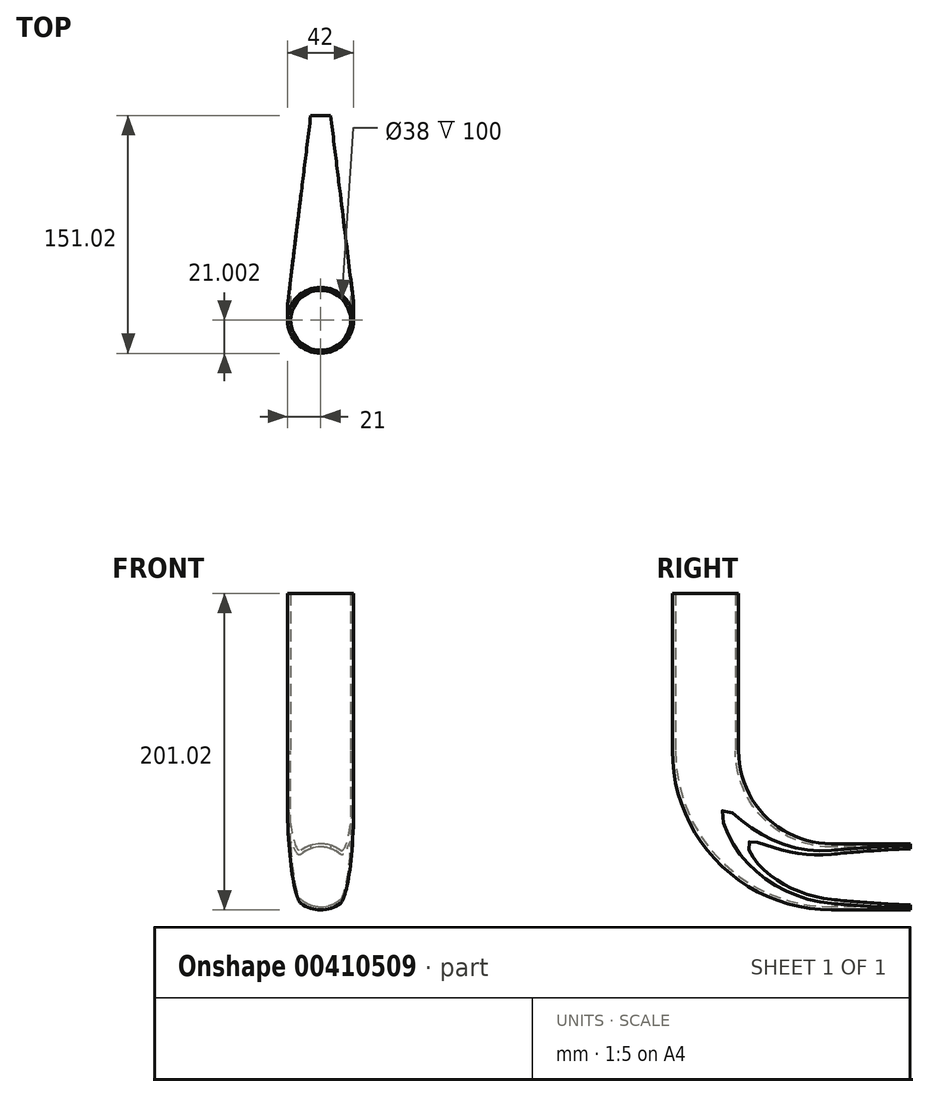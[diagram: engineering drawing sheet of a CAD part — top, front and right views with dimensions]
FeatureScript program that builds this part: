
annotation { "Feature Type Name" : "Feature", "Feature Type Description" : "" }
export const myFeature = defineFeature(function(context is Context, id is Id, definition is map)
    precondition{}
    {
        {
            var Q0;
            Q0=qCreatedBy(makeId("Right.planeOp"),FACE);
            var sketch = newSketch(context, id + "F0", { "sketchPlane" : qUnion([Q0])});
            skArc(sketch, "E0", {"start": v(0, -80) * mm, "mid": v(-56.57, -56.57) * mm, "end": v(-80, 0) * mm});
            skSolve(sketch);
        }
        {
            var Q0;
            Q0=qCreatedBy(makeId("Top.planeOp"),FACE);
            var sketch = newSketch(context, id + "F1", { "sketchPlane" : qUnion([Q0])});
            skCircle(sketch, "E1", {"center": v(0, -80.02) * mm, "radius": 21 * mm});
            skCircle(sketch, "E2", {"center": v(0, -80.02) * mm, "radius": 19 * mm});
            skSolve(sketch);
        }
        {
            var Q0;
            Q0=makeQuery(id+"F1.imprint","IMPRINT",FACE,{"disambiguationData":[TD([[makeQuery(id+"F1.imprint","IMPRINT",EDGE,{"derivedFrom":sQuery(id+"F1.wireOp",EDGE,"E1")}),1.0]])]});
            var Q1;
            Q1=sQuery(id+"F0.wireOp",EDGE,"E0");
            sweep(context, id + "F2", {"profiles" : qUnion([Q0]), "path" : qUnion([Q1])});
        }
        {
            var Q0;
            Q0=makeQuery(id+"F2.opSweep","CAP_FACE",FACE,{"disambiguationData":[OSD([sQuery(id+"F0.wireOp",VERTEX,"E0.end"),sQuery(id+"F1.wireOp",EDGE,"E1"),sQuery(id+"F1.wireOp",EDGE,"E2")])],"isStart":true});
            extrude(context, id + "F3", {"entities" : qUnion([Q0]), "operationType" : NewBodyOperationType.ADD, "depth" : 100 * mm});
        }
        {
            var Q0;
            Q0=makeQuery(id+"F2.opSweep","CAP_FACE",FACE,{"disambiguationData":[OSD([sQuery(id+"F0.wireOp",VERTEX,"E0.start"),sQuery(id+"F1.wireOp",EDGE,"E1"),sQuery(id+"F1.wireOp",EDGE,"E2")])],"isStart":false});
            extrude(context, id + "F4", {"entities" : qUnion([Q0]), "operationType" : NewBodyOperationType.ADD, "depth" : 50 * mm});
        }
        {
            var Q0;
            Q0=makeQuery(id+"F4.opExtrude","SWEPT_FACE",FACE,{"disambiguationData":[OSD([sQuery(id+"F0.wireOp",VERTEX,"E0.start"),sQuery(id+"F1.wireOp",EDGE,"E2")])]});
            cPlane(context, id + "F5", {"entities" : qUnion([Q0]), "cplaneType" : CPlaneType.LINE_ANGLE, "offset" : 25 * mm, "angle" : 0 * degree, "width" : 150 * mm, "height" : 150 * mm});
        }
        {
            var Q0;
            Q0=qCreatedBy(id+"F5.planeOp",FACE);
            var sketch = newSketch(context, id + "F6", { "sketchPlane" : qUnion([Q0])});
            skLineSegment(sketch, "E3", {"start": v(-6.33, 50) * mm, "end": v(-30.9, -150) * mm});
            skLineSegment(sketch, "E4", {"start": v(-30.9, -150) * mm, "end": v(-50, -150) * mm});
            skLineSegment(sketch, "E5", {"start": v(-50, -150) * mm, "end": v(-50, 50) * mm});
            skLineSegment(sketch, "E6", {"start": v(-50, 50) * mm, "end": v(-6.33, 50) * mm});
            skLineSegment(sketch, "E7.0", {"start": v(19, 50) * mm, "end": v(-19, 50) * mm});
            skLineSegment(sketch, "E8.MirrorCS", {"start": v(50, 50) * mm, "end": v(6.33, 50) * mm});
            skSolve(sketch);
        }
        {
            var Q0;
            Q0=qSketchRegion(id+"F6",true);
            extrude(context, id + "F7", {"entities" : qUnion([Q0]), "depth" : 200 * mm, "symmetric" : true});
        }
        {
            var Q0;
            Q0=makeQuery(id+"F7.opExtrude","SWEPT_BODY",BODY,{"disambiguationData":[OSD([sQuery(id+"F6.wireOp",EDGE,"E3"),sQuery(id+"F6.wireOp",EDGE,"E4"),sQuery(id+"F6.wireOp",EDGE,"E5"),sQuery(id+"F6.wireOp",EDGE,"E6"),sQuery(id+"F6.wireOp",EDGE,"E7.0")])]});
            var Q1;
            Q1=qCreatedBy(makeId("Right.planeOp"),FACE);
            mirror(context, id + "F8", {"entities" : qUnion([Q0]), "mirrorPlane" : qUnion([Q1])});
        }
        {
            var Q0;
            Q0=makeQuery(id+"F8.opPattern","COPY",BODY,{"derivedFrom":makeQuery(id+"F7.opExtrude","SWEPT_BODY",BODY,{"disambiguationData":[OSD([sQuery(id+"F6.wireOp",EDGE,"E3"),sQuery(id+"F6.wireOp",EDGE,"E4"),sQuery(id+"F6.wireOp",EDGE,"E5"),sQuery(id+"F6.wireOp",EDGE,"E6"),sQuery(id+"F6.wireOp",EDGE,"E7.0")])]}),"instanceName":"1"});
            var Q1;
            Q1=makeQuery(id+"F7.opExtrude","SWEPT_BODY",BODY,{"disambiguationData":[OSD([sQuery(id+"F6.wireOp",EDGE,"E3"),sQuery(id+"F6.wireOp",EDGE,"E4"),sQuery(id+"F6.wireOp",EDGE,"E5"),sQuery(id+"F6.wireOp",EDGE,"E6"),sQuery(id+"F6.wireOp",EDGE,"E7.0")])]});
            var Q2;
            Q2=makeQuery(id+"F2.opSweep","SWEPT_BODY",BODY,{"disambiguationData":[OSD([sQuery(id+"F0.wireOp",EDGE,"E0"),sQuery(id+"F1.wireOp",EDGE,"E1"),sQuery(id+"F1.wireOp",EDGE,"E2")])]});
            booleanBodies(context, id + "F9", {"operationType" : BooleanOperationType.SUBTRACTION, "tools" : qUnion([Q0, Q1]), "targets" : qUnion([Q2])});
        }
    });
